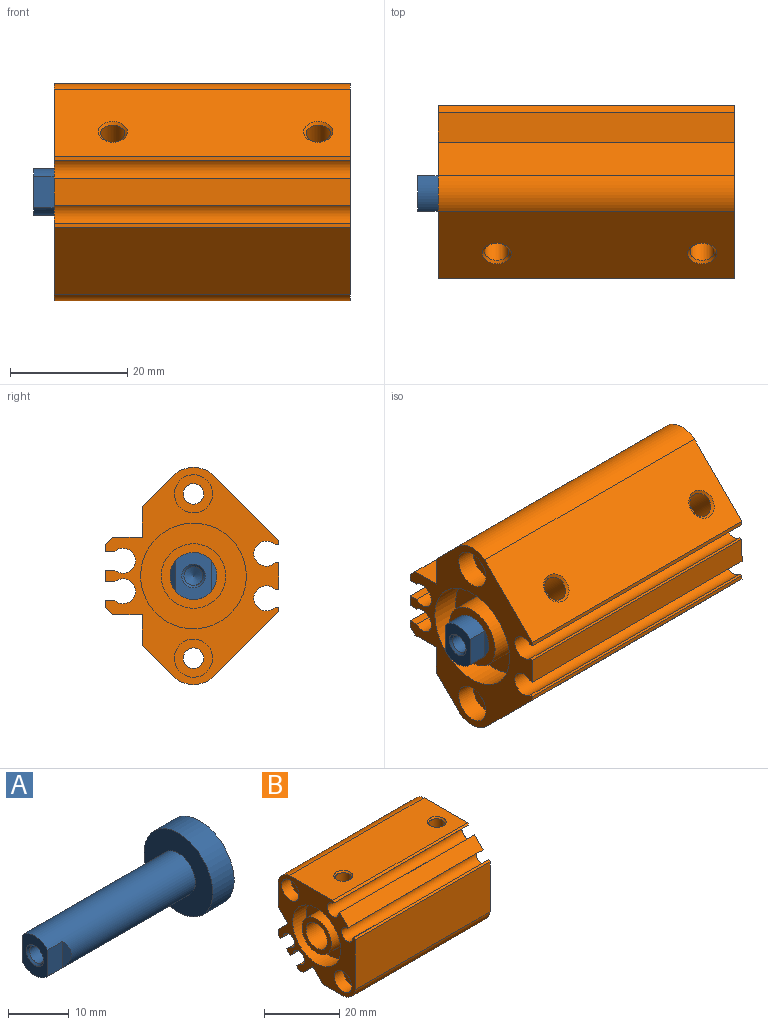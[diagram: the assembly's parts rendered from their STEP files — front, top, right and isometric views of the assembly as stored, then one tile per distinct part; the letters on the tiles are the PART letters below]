
ASSEMBLY  parts=2 mates=1
PART A: 12 faces, bbox 38.5x16x16 mm
  f0: cone r=866.03mm half-angle=60deg, axis (-1,0,0), area 9.5mm2, adj f1
  f1: cylinder r=1.62mm len=7.62mm, axis (-1,0,0), area 77.6mm2, adj f0,f4
  f2: cylinder r=4mm len=33.5mm, axis (-1,0,0), area 793.8mm2, adj f3,f5,f8,f9,f10,f11
  f3: plane 8x6mm, normal (-1,0,0), area 30.4mm2, adj f2,f4,f9,f10
  f4: cone r=1.62mm half-angle=45deg, axis (-1,0,0), area 6.1mm2, adj f1,f3
  f5: plane 16x16mm, normal (-1,0,0), area 150.8mm2, adj f2,f6
  f6: cylinder r=8mm len=16mm, axis (-1,0,0), area 251.3mm2, adj f5,f7
  f7: plane 16x16mm, normal (1,0,0), area 201.1mm2, adj f6
  f8: plane 5.29x1mm, normal (-0.71,-0.71,0), area 5.1mm2, adj f2,f9
  f9: plane 5.29x3.5mm, normal (0,-1,0), area 18.5mm2, adj f2,f3,f8
  f10: plane 5.29x3.5mm, normal (0,1,0), area 18.5mm2, adj f2,f3,f11
  f11: plane 5.29x1mm, normal (-0.71,0.71,0), area 5.1mm2, adj f2,f10
PART B: 58 faces, bbox 50.5x29x29 mm
  f0: plane 50.5x0.42mm, normal (0,0.71,0.71), area 29.7mm2, adj f1,f2,f3,f34
  f1: plane 29x29mm, normal (1,0,0), area 351.6mm2, adj f0,f2,f3,f4,f5,f6,f7,f8
  f2: cylinder r=2.13mm len=50.5mm, axis (1,0,0), area 507.8mm2, adj f0,f1,f30,f34
  f3: plane 50.5x0.5mm, normal (0,-0.71,0.71), area 35.7mm2, adj f0,f1,f4,f34
  f4: plane 50.5x16.23mm, normal (0,-1,0), area 819.5mm2, adj f1,f3,f5,f34
  f5: cylinder r=5mm len=50.5mm, axis (1,0,0), area 328.1mm2, adj f1,f4,f6,f34
  f6: plane 50.5x8.03mm, normal (0,0,-1), area 405.3mm2, adj f1,f5,f7,f34
  f7: plane 50.5x3.68mm, normal (0,0.71,-0.71), area 262.9mm2, adj f1,f6,f8,f34
  f8: plane 50.5x3.61mm, normal (0,-0.71,-0.71), area 257.5mm2, adj f1,f7,f9,f34
  f9: plane 50.5x1.7mm, normal (0,0,-1), area 85.7mm2, adj f1,f8,f10,f34
  f10: plane 50.5x0.85mm, normal (0,0.71,-0.71), area 60.6mm2, adj f1,f9,f11,f34
  f11: plane 50.5x1.13mm, normal (0,0.71,0.71), area 80.5mm2, adj f1,f10,f12,f34
  f12: cylinder r=2.13mm len=50.5mm, axis (1,0,0), area 493mm2, adj f1,f11,f13,f34
  f13: plane 50.5x1.13mm, normal (0,-0.71,-0.71), area 80.5mm2, adj f1,f12,f14,f34
  f14: plane 50.5x1.41mm, normal (0,0.71,-0.71), area 101mm2, adj f1,f13,f15,f34
  f15: plane 50.5x1.13mm, normal (0,0.71,0.71), area 80.5mm2, adj f1,f14,f16,f34
  f16: cylinder r=2.13mm len=50.5mm, axis (1,0,0), area 493mm2, adj f1,f15,f17,f34
  f17: plane 50.5x1.13mm, normal (0,-0.71,-0.71), area 80.5mm2, adj f1,f16,f18,f34
  f18: plane 50.5x0.85mm, normal (0,0.71,-0.71), area 60.6mm2, adj f1,f17,f19,f34
  f19: plane 50.5x1.7mm, normal (0,1,0), area 85.7mm2, adj f1,f18,f20,f34
  f20: plane 50.5x3.61mm, normal (0,0.71,0.71), area 257.5mm2, adj f1,f19,f21,f34
  f21: plane 50.5x3.68mm, normal (0,0.71,-0.71), area 262.9mm2, adj f1,f20,f22,f34
  f22: plane 50.5x8.03mm, normal (0,1,0), area 405.3mm2, adj f1,f21,f23,f34
  f23: cylinder r=5mm len=50.5mm, axis (1,0,0), area 328.1mm2, adj f1,f22,f24,f34
  f24: plane 50.5x16.23mm, normal (0,0,1), area 780.3mm2, adj f1,f23,f25,f34,f42,f45
  f25: plane 50.5x0.5mm, normal (0,-0.71,0.71), area 35.7mm2, adj f1,f24,f26,f34
  f26: plane 50.5x0.42mm, normal (0,-0.71,-0.71), area 29.7mm2, adj f1,f25,f27,f34
  f27: cylinder r=2.13mm len=50.5mm, axis (1,0,0), area 507.8mm2, adj f1,f26,f28,f34
  f28: plane 50.5x0.42mm, normal (0,0.71,0.71), area 29.7mm2, adj f1,f27,f29,f34
  f29: plane 50.5x3.25mm, normal (0,-0.71,0.71), area 232.3mm2, adj f1,f28,f30,f34
  f30: plane 50.5x0.42mm, normal (0,-0.71,-0.71), area 29.7mm2, adj f1,f2,f29,f34
  f31: cylinder r=9mm len=18mm, axis (-1,0,0), area 84.8mm2, adj f1,f33
  f32: cylinder r=5.5mm len=11mm, axis (1,0,0), area 172.8mm2, adj f35,f37
  f33: plane 18x18mm, normal (1,0,0), area 254.5mm2, adj f31
  f34: plane 29x29mm, normal (-1,0,0), area 351.6mm2, adj f0,f2,f3,f4,f5,f6,f7,f8
  f35: plane 11x11mm, normal (-1,0,0), area 44.8mm2, adj f32,f36
  f36: cylinder r=4mm len=10mm, axis (-1,0,0), area 251.3mm2, adj f35,f39
  f37: plane 18x18mm, normal (-1,0,0), area 159.4mm2, adj f32,f38
  f38: cylinder r=9mm len=18mm, axis (1,0,0), area 282.7mm2, adj f34,f37
  f39: plane 16x16mm, normal (1,0,0), area 150.8mm2, adj f36,f40
  f40: cylinder r=8mm len=25mm, axis (-1,0,0), area 1256.6mm2, adj f39,f41
  f41: plane 16x16mm, normal (-1,0,0), area 201.1mm2, adj f40
  f42: cone r=2.5mm half-angle=45deg, axis (0,0,1), area 8.8mm2, adj f24,f43
  f43: cylinder r=2.07mm len=5.57mm, axis (0,0,1), area 72.3mm2, adj f42,f44
  f44: plane 4.13x4.13mm, normal (0,0,1), area 13.4mm2, adj f43
  f45: cone r=2.5mm half-angle=45deg, axis (0,0,1), area 8.8mm2, adj f24,f46
  f46: cylinder r=2.07mm len=5.57mm, axis (0,0,1), area 72.3mm2, adj f45,f47
  f47: plane 4.13x4.13mm, normal (0,0,1), area 13.4mm2, adj f46
  f48: cylinder r=3.25mm len=6.5mm, axis (-1,0,0), area 71.5mm2, adj f34,f49
  f49: plane 6.5x6.5mm, normal (-1,0,0), area 23.6mm2, adj f48,f50
  f50: cylinder r=1.75mm len=43.5mm, axis (-1,0,0), area 478.3mm2, adj f49,f51
  f51: plane 6.5x6.5mm, normal (1,0,0), area 23.6mm2, adj f50,f52
  f52: cylinder r=3.25mm len=6.5mm, axis (-1,0,0), area 71.5mm2, adj f1,f51
  f53: cylinder r=3.25mm len=6.5mm, axis (-1,0,0), area 71.5mm2, adj f34,f54
  f54: plane 6.5x6.5mm, normal (-1,0,0), area 23.6mm2, adj f53,f55
  f55: cylinder r=1.75mm len=43.5mm, axis (-1,0,0), area 478.3mm2, adj f54,f56
  f56: plane 6.5x6.5mm, normal (1,0,0), area 23.6mm2, adj f55,f57
  f57: cylinder r=3.25mm len=6.5mm, axis (-1,0,0), area 71.5mm2, adj f1,f56
PLACE A t=(-43.73,1.51,-32.57)mm
PLACE B rot(axis=(1,0,0),45deg) t=(-43.73,1.51,-32.57)mm
MATE slider B.f31 <-> A.f0  axis (-1,0,0) through (-8.73,1.51,-32.57)mm
